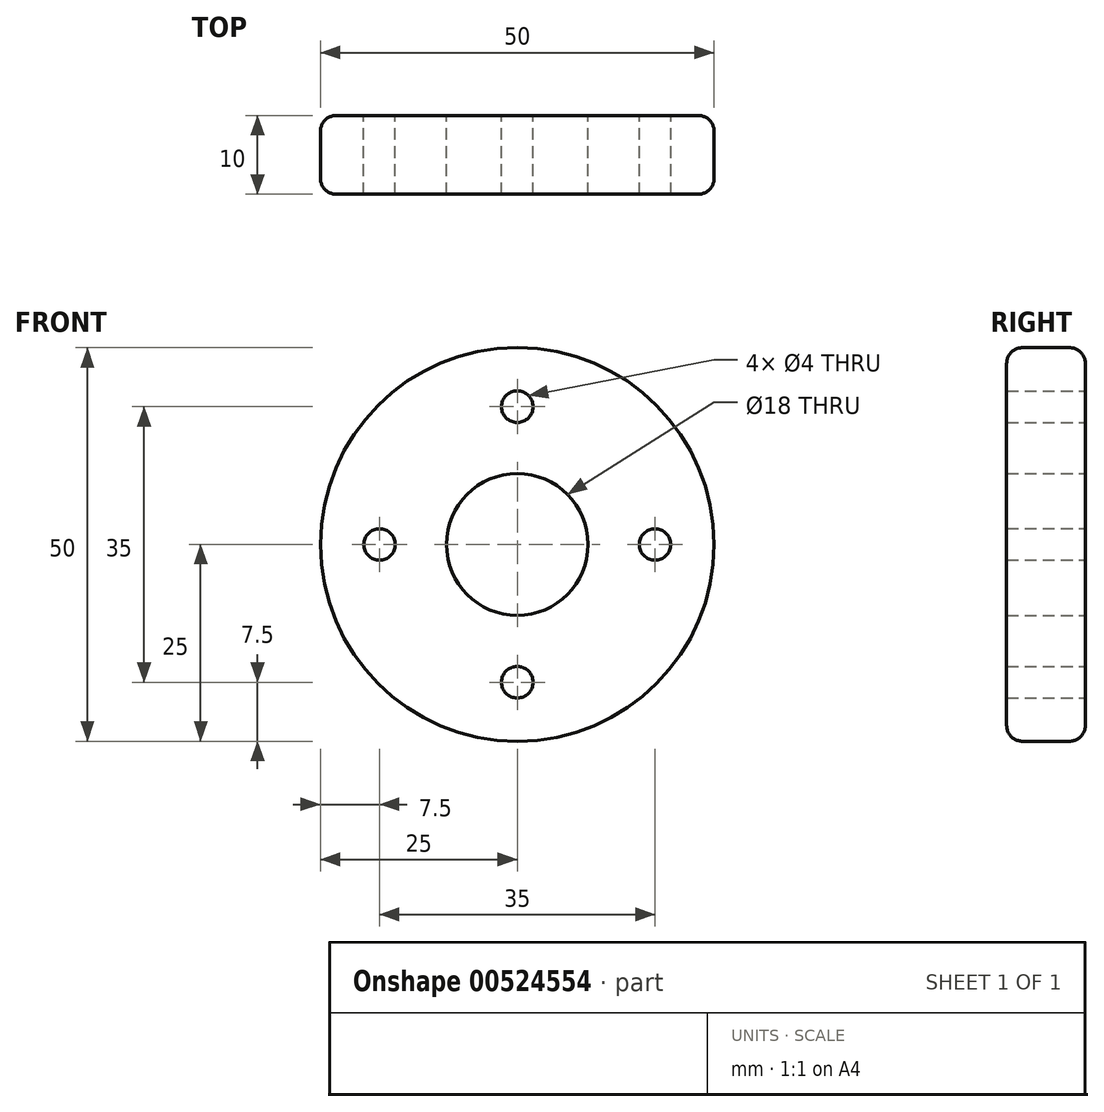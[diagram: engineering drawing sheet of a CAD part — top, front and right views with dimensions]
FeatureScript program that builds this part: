
annotation { "Feature Type Name" : "Feature", "Feature Type Description" : "" }
export const myFeature = defineFeature(function(context is Context, id is Id, definition is map)
    precondition{}
    {
        {
            var Q0;
            Q0=qCreatedBy(makeId("Front.planeOp"),FACE);
            var sketch = newSketch(context, id + "F0", { "sketchPlane" : qUnion([Q0])});
            skCircle(sketch, "E0", {"center": v(0, 0) * mm, "radius": 25 * mm});
            skCircle(sketch, "E1", {"center": v(0, 0) * mm, "radius": 17.5 * mm, "construction": true});
            skCircle(sketch, "E2", {"center": v(0, 17.5) * mm, "radius": 2 * mm});
            skCircle(sketch, "E3", {"center": v(17.5, 0) * mm, "radius": 2 * mm});
            skCircle(sketch, "E4", {"center": v(0, -17.5) * mm, "radius": 2 * mm});
            skCircle(sketch, "E5", {"center": v(-17.5, 0) * mm, "radius": 2 * mm});
            skCircle(sketch, "E6", {"center": v(0, 0) * mm, "radius": 9 * mm});
            skSolve(sketch);
        }
        {
            var Q0;
            Q0 = qSketchRegion(id + "F0", true);
            extrude(context, id + "F1", {"entities" : qUnion([Q0]), "depth" : 10 * mm, "offsetDistance" : 25.4 * mm});
        }
        {
            var Q0;
            Q0=makeQuery(id+"F1.opExtrude","SWEPT_FACE",FACE,{"disambiguationData":[OSD([sQuery(id+"F0.wireOp",EDGE,"E0")])]});
            var Q1;
            Q1=makeQuery(id+"F1.opExtrude","CAP_EDGE",EDGE,{"disambiguationData":[OSD([sQuery(id+"F0.wireOp",EDGE,"E0")])],"isStart":false});
            fillet(context, id + "F2", {"entities" : qUnion([Q0, Q1]), "radius" : 2 * mm, "tangentPropagation" : true, "allowEdgeOverflow" : false});
        }
    });
